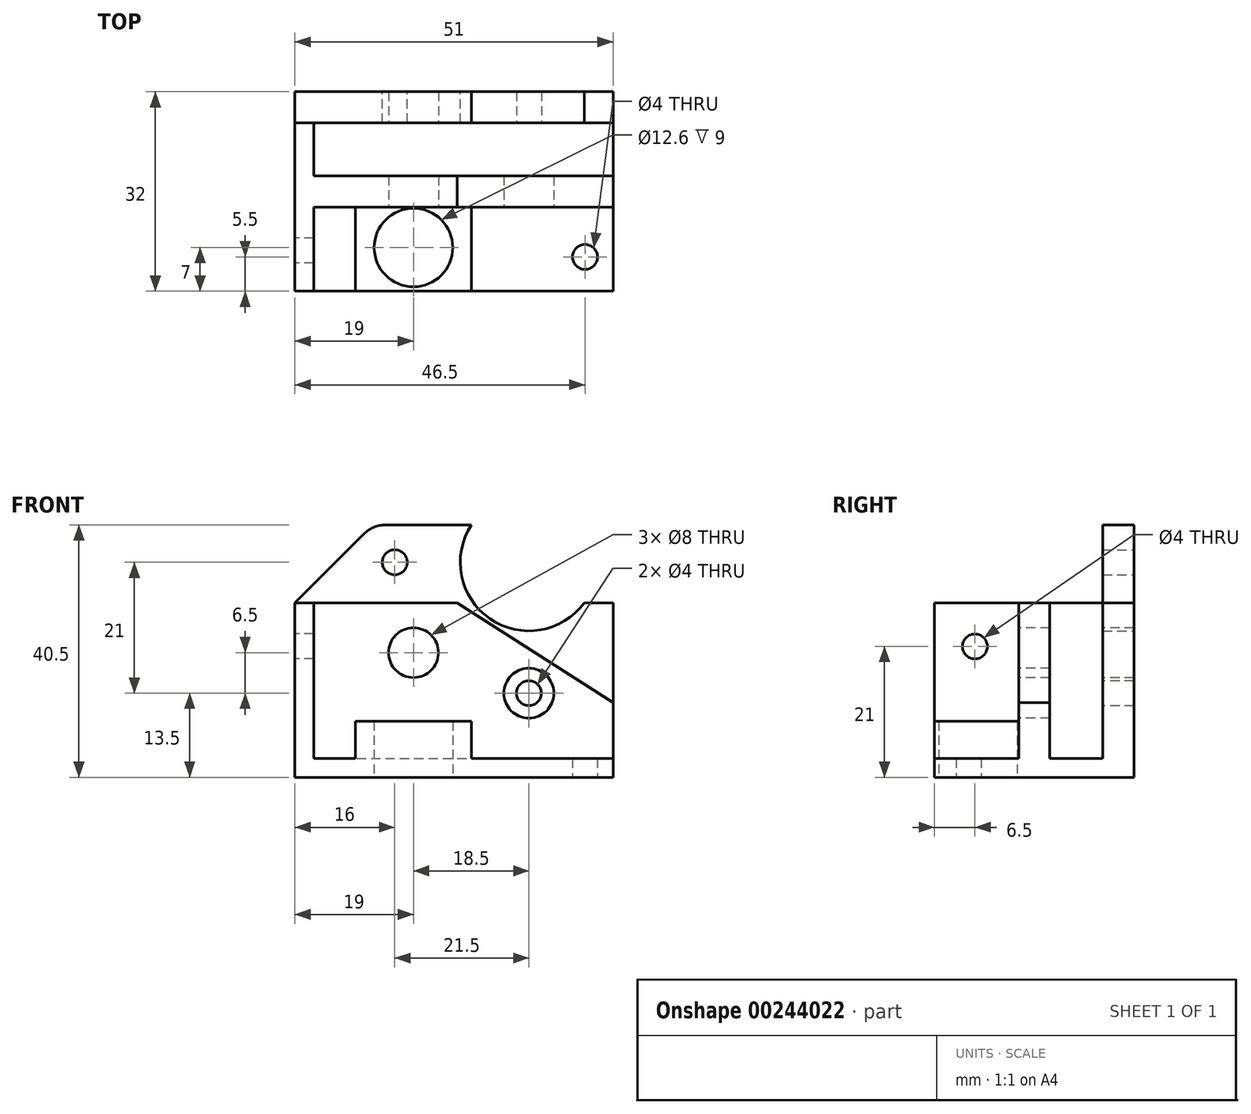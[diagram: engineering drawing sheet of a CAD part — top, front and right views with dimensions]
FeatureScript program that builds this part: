
annotation { "Feature Type Name" : "Feature", "Feature Type Description" : "" }
export const myFeature = defineFeature(function(context is Context, id is Id, definition is map)
    precondition{}
    {
        {
            var Q0;
            Q0=qCreatedBy(makeId("Top.planeOp"),FACE);
            var sketch = newSketch(context, id + "F0", { "sketchPlane" : qUnion([Q0])});
            skLineSegment(sketch, "E0.bottom", {"start": v(-25.5, 16) * mm, "end": v(25.5, 16) * mm});
            skLineSegment(sketch, "E0.top", {"start": v(-25.5, -16) * mm, "end": v(25.5, -16) * mm});
            skLineSegment(sketch, "E0.left", {"start": v(-25.5, 16) * mm, "end": v(-25.5, -16) * mm});
            skLineSegment(sketch, "E0.right", {"start": v(25.5, 16) * mm, "end": v(25.5, -16) * mm});
            skPoint(sketch, "E0.middle", {"position": v(0, 0) * mm});
            skCircle(sketch, "E1", {"center": v(21, -10.5) * mm, "radius": 2 * mm});
            skSolve(sketch);
        }
        {
            var Q0;
            Q0=makeQuery(id+"F0.imprint","IMPRINT",FACE,{"disambiguationData":[TD([[makeQuery(id+"F0.imprint","IMPRINT",EDGE,{"derivedFrom":sQuery(id+"F0.wireOp",EDGE,"E0.bottom")}),-1.0]])]});
            extrude(context, id + "F1", {"entities" : qUnion([Q0]), "depth" : 3 * mm});
        }
        {
            var Q0;
            Q0=makeQuery(id+"F1.opExtrude","CAP_FACE",FACE,{"disambiguationData":[OSD([sQuery(id+"F0.wireOp",EDGE,"E0.bottom"),sQuery(id+"F0.wireOp",EDGE,"E0.top"),sQuery(id+"F0.wireOp",EDGE,"E0.left"),sQuery(id+"F0.wireOp",EDGE,"E0.right"),sQuery(id+"F0.wireOp",EDGE,"E1")])],"isStart":false});
            var sketch = newSketch(context, id + "F2", { "sketchPlane" : qUnion([Q0])});
            skLineSegment(sketch, "E2", {"start": v(-22.5, 11) * mm, "end": v(25.5, 11) * mm});
            skLineSegment(sketch, "E3", {"start": v(-22.5, 2.5) * mm, "end": v(25.5, 2.5) * mm});
            skLineSegment(sketch, "E4.trimOffspring", {"start": v(-22.5, 2.5) * mm, "end": v(-22.5, 11) * mm});
            skLineSegment(sketch, "E5", {"start": v(-15.8, -2.5) * mm, "end": v(-15.8, -16) * mm});
            skLineSegment(sketch, "E6", {"start": v(2.8, -16) * mm, "end": v(2.8, -2.5) * mm});
            skLineSegment(sketch, "E7", {"start": v(-22.5, -2.5) * mm, "end": v(-22.5, -16) * mm});
            skLineSegment(sketch, "E8", {"start": v(-22.5, -2.5) * mm, "end": v(25.5, -2.5) * mm});
            skCircle(sketch, "E9", {"center": v(-6.5, -9) * mm, "radius": 6.3 * mm});
            skSolve(sketch);
        }
        {
            var Q0;
            {var subQ10=sQuery(id+"F2.wireOp",EDGE,"E2");Q0=makeQuery(id+"F2.imprint","IMPRINT",FACE,{"disambiguationData":[TD([[makeQuery(id+"F2.imprint","IMPRINT",EDGE,{"derivedFrom":subQ10}),1.0]])]});}
            extrude(context, id + "F3", {"entities" : qUnion([Q0]), "operationType" : NewBodyOperationType.ADD, "depth" : 25 * mm});
        }
        {
            var Q0;
            {var subQ1=sQuery(id+"F2.wireOp",EDGE,"E5");Q0=makeQuery(id+"F2.imprint","IMPRINT",FACE,{"disambiguationData":[TD([[makeQuery(id+"F2.imprint","IMPRINT",EDGE,{"derivedFrom":subQ1}),1.0]])]});}
            extrude(context, id + "F4", {"entities" : qUnion([Q0]), "operationType" : NewBodyOperationType.ADD, "depth" : 6 * mm});
        }
        {
            var Q0;
            {var subQ0=sQuery(id+"F0.wireOp",EDGE,"E1");var subQ1=sQuery(id+"F0.wireOp",EDGE,"E0.right");var subQ4=sQuery(id+"F0.wireOp",EDGE,"E0.top");var subQ5=sQuery(id+"F0.wireOp",EDGE,"E0.bottom");Q0=makeQuery(id+"F4.boolean.opBoolean","SPLIT",FACE,{"disambiguationData":[TD([makeQuery(id+"F4.opExtrude","SWEPT_FACE",FACE,{"disambiguationData":[OSD([sQuery(id+"F2.wireOp",EDGE,"E9")])]})])],"derivedFrom":makeQuery(id+"F3.boolean.opBoolean","SPLIT",FACE,{"disambiguationData":[TD([makeQuery(id+"F1.opExtrude","SWEPT_FACE",FACE,{"disambiguationData":[OSD([subQ4])]})])],"derivedFrom":makeQuery(id+"F1.opExtrude","CAP_FACE",FACE,{"disambiguationData":[OSD([subQ5,subQ4,sQuery(id+"F0.wireOp",EDGE,"E0.left"),subQ1,subQ0])],"isStart":false})})});}
            extrude(context, id + "F5", {"entities" : qUnion([Q0]), "operationType" : NewBodyOperationType.REMOVE, "endBound" : BoundingType.UP_TO_NEXT, "oppositeDirection" : true, "depth" : 25 * mm});
        }
        {
            var Q0;
            {var subQ0=sQuery(id+"F0.wireOp",EDGE,"E0.right");var subQ1=makeQuery(id+"F1.opExtrude","CAP_EDGE",EDGE,{"disambiguationData":[OSD([subQ0])],"isStart":false});Q0=makeQuery(id+"F3.opExtrude","CAP_EDGE",EDGE,{"disambiguationData":[OSD([subQ0]),TDD([makeQuery(id+"F2.imprint","IMPRINT",EDGE,{"disambiguationData":[TD([[makeQuery(id+"F2.imprint","INTERSECT",VERTEX,{"derivedFrom":[subQ1,sQuery(id+"F2.wireOp",EDGE,"E3")]}),-1.0]])],"derivedFrom":subQ1})])],"isStart":false});}
            chamfer(context, id + "F6", {"entities" : qUnion([Q0]), "chamferType" : ChamferType.TWO_OFFSETS, "width1" : 16 * mm, "oppositeDirection" : false, "width2" : 25 * mm, "tangentPropagation" : true});
        }
        {
            var Q0;
            Q0=makeQuery(id+"F3.opExtrude","SWEPT_FACE",FACE,{"disambiguationData":[OSD([sQuery(id+"F2.wireOp",EDGE,"E8")])]});
            var sketch = newSketch(context, id + "F7", { "sketchPlane" : qUnion([Q0])});
            skCircle(sketch, "E10", {"center": v(-6.5, 20) * mm, "radius": 4 * mm});
            skCircle(sketch, "E11", {"center": v(12, 13.5) * mm, "radius": 4 * mm});
            skCircle(sketch, "E12", {"center": v(12, 13.5) * mm, "radius": 2 * mm});
            skSolve(sketch);
        }
        {
            var Q0;
            Q0=makeQuery(id+"F7.imprint","IMPRINT",FACE,{"disambiguationData":[TD([[makeQuery(id+"F7.imprint","IMPRINT",EDGE,{"derivedFrom":sQuery(id+"F7.wireOp",EDGE,"E10")}),1.0]])]});
            extrude(context, id + "F8", {"entities" : qUnion([Q0]), "operationType" : NewBodyOperationType.REMOVE, "endBound" : BoundingType.THROUGH_ALL, "oppositeDirection" : true, "depth" : 25 * mm});
        }
        {
            var Q0;
            Q0=makeQuery(id+"F7.imprint","IMPRINT",FACE,{"disambiguationData":[TD([[makeQuery(id+"F7.imprint","IMPRINT",EDGE,{"derivedFrom":sQuery(id+"F7.wireOp",EDGE,"E12")}),1.0]])]});
            extrude(context, id + "F9", {"entities" : qUnion([Q0]), "operationType" : NewBodyOperationType.REMOVE, "endBound" : BoundingType.THROUGH_ALL, "oppositeDirection" : true, "depth" : 25 * mm});
        }
        {
            var Q0;
            Q0=makeQuery(id+"F7.imprint","IMPRINT",FACE,{"disambiguationData":[TD([[makeQuery(id+"F7.imprint","IMPRINT",EDGE,{"derivedFrom":sQuery(id+"F7.wireOp",EDGE,"E11")}),1.0]])]});
            extrude(context, id + "F10", {"entities" : qUnion([Q0]), "operationType" : NewBodyOperationType.REMOVE, "endBound" : BoundingType.UP_TO_NEXT, "oppositeDirection" : true, "depth" : 25 * mm});
        }
        {
            var Q0;
            Q0=makeQuery(id+"F3.opExtrude","CAP_FACE",FACE,{"disambiguationData":[OSD([sQuery(id+"F0.wireOp",EDGE,"E0.bottom"),sQuery(id+"F0.wireOp",EDGE,"E0.top"),sQuery(id+"F0.wireOp",EDGE,"E0.left"),sQuery(id+"F0.wireOp",EDGE,"E0.right"),sQuery(id+"F2.wireOp",EDGE,"E2"),sQuery(id+"F2.wireOp",EDGE,"E3"),sQuery(id+"F2.wireOp",EDGE,"E4.trimOffspring"),sQuery(id+"F2.wireOp",EDGE,"E7"),sQuery(id+"F2.wireOp",EDGE,"E8")])],"isStart":false});
            var sketch = newSketch(context, id + "F11", { "sketchPlane" : qUnion([Q0])});
            skLineSegment(sketch, "E13", {"start": v(-22.5, 11) * mm, "end": v(-25.5, 11) * mm});
            skSolve(sketch);
        }
        {
            var Q0;
            {var subQ5=sQuery(id+"F11.wireOp",EDGE,"E13");Q0=makeQuery(id+"F11.imprint","IMPRINT",FACE,{"disambiguationData":[TD([[makeQuery(id+"F11.imprint","IMPRINT",EDGE,{"derivedFrom":subQ5}),-1.0]])]});}
            extrude(context, id + "F12", {"entities" : qUnion([Q0]), "operationType" : NewBodyOperationType.ADD, "depth" : 12.5 * mm});
        }
        {
            var Q0;
            {var subQ0=sQuery(id+"F0.wireOp",EDGE,"E0.bottom");Q0=makeQuery(id+"F12.boolean.opBoolean","MERGE",FACE,{"derivedFrom":[makeQuery(id+"F3.boolean.opBoolean","MERGE",FACE,{"derivedFrom":[makeQuery(id+"F1.opExtrude","SWEPT_FACE",FACE,{"disambiguationData":[OSD([subQ0])]}),makeQuery(id+"F3.opExtrude","SWEPT_FACE",FACE,{"disambiguationData":[OSD([subQ0])]})]}),makeQuery(id+"F12.opExtrude","SWEPT_FACE",FACE,{"disambiguationData":[OSD([subQ0])]})]});}
            var sketch = newSketch(context, id + "F13", { "sketchPlane" : qUnion([Q0])});
            skCircle(sketch, "E14", {"center": v(9.5, 34.5) * mm, "radius": 2 * mm});
            skLineSegment(sketch, "E15", {"start": v(-12, 13.5) * mm, "end": v(-12, 47.77) * mm, "construction": true});
            skArc(sketch, "E16", {"start": v(-20.87, 28) * mm, "mid": v(-5.75, 25.45) * mm, "end": v(-2.78, 40.5) * mm});
            skLineSegment(sketch, "E17", {"start": v(-25.5, 28) * mm, "end": v(-20.87, 28) * mm});
            skPoint(sketch, "E18", {"position": v(-2.78, 40.5) * mm});
            skSolve(sketch);
        }
        {
            var Q0;
            Q0=makeQuery(id+"F13.imprint","IMPRINT",FACE,{"disambiguationData":[TD([[makeQuery(id+"F13.imprint","IMPRINT",EDGE,{"derivedFrom":sQuery(id+"F13.wireOp",EDGE,"E14")}),1.0]])]});
            var Q1;
            {var subQ0=sQuery(id+"F13.wireOp",EDGE,"E16");var subQ1=makeQuery(id+"F13.imprint","INTERSECT",VERTEX,{"derivedFrom":[subQ0,sQuery(id+"F13.wireOp",EDGE,"E17")]});Q1=makeQuery(id+"F13.imprint","IMPRINT",FACE,{"disambiguationData":[TD([[makeQuery(id+"F13.imprint","IMPRINT",EDGE,{"disambiguationData":[TD([[subQ1,1.0]])],"derivedFrom":subQ0}),1.0]])]});}
            var Q2;
            {var subQ0=sQuery(id+"F13.wireOp",EDGE,"E17");Q2=makeQuery(id+"F13.imprint","IMPRINT",FACE,{"disambiguationData":[TD([[makeQuery(id+"F13.imprint","IMPRINT",EDGE,{"derivedFrom":subQ0}),1.0]])]});}
            extrude(context, id + "F14", {"entities" : qUnion([Q0, Q1, Q2]), "operationType" : NewBodyOperationType.REMOVE, "endBound" : BoundingType.UP_TO_NEXT, "oppositeDirection" : true, "depth" : 25 * mm});
        }
        {
            var Q0;
            Q0=makeQuery(id+"F12.opExtrude","CAP_EDGE",EDGE,{"disambiguationData":[OSD([sQuery(id+"F0.wireOp",EDGE,"E0.left")])],"isStart":false});
            chamfer(context, id + "F15", {"entities" : qUnion([Q0]), "width" : 12.5 * mm, "tangentPropagation" : true});
        }
        {
            var Q0;
            Q0=makeQuery(id+"F14.boolean.opBoolean","COPY",EDGE,{"derivedFrom":makeQuery(id+"F14.opExtrude","SWEPT_EDGE",EDGE,{"disambiguationData":[OSD([sQuery(id+"F0.wireOp",EDGE,"E0.bottom"),sQuery(id+"F13.wireOp",EDGE,"E16")])]})});
            var Q1;
            {var subQ0=sQuery(id+"F0.wireOp",EDGE,"E0.left");Q1=makeQuery(id+"F15.opChamfer","BLEND_EDGE",EDGE,{"blendedFrom":[makeQuery(id+"F12.opExtrude","CAP_EDGE",EDGE,{"disambiguationData":[OSD([subQ0])],"isStart":false}),makeQuery(id+"F12.opExtrude","CAP_FACE",FACE,{"disambiguationData":[OSD([sQuery(id+"F0.wireOp",EDGE,"E0.bottom"),subQ0,sQuery(id+"F0.wireOp",EDGE,"E0.right"),sQuery(id+"F2.wireOp",EDGE,"E2"),sQuery(id+"F11.wireOp",EDGE,"E13")])],"isStart":false})],"blendedInto":[makeQuery(id+"F12.opExtrude","CAP_FACE",FACE,{"disambiguationData":[OSD([sQuery(id+"F0.wireOp",EDGE,"E0.bottom"),subQ0,sQuery(id+"F0.wireOp",EDGE,"E0.right"),sQuery(id+"F2.wireOp",EDGE,"E2"),sQuery(id+"F11.wireOp",EDGE,"E13")])],"isStart":false})]});}
            fillet(context, id + "F16", {"entities" : qUnion([Q0, Q1]), "radius" : 5 * mm, "tangentPropagation" : true, "allowEdgeOverflow" : false});
        }
        {
            var Q0;
            {var subQ0=sQuery(id+"F0.wireOp",EDGE,"E0.left");Q0=makeQuery(id+"F12.boolean.opBoolean","MERGE",FACE,{"derivedFrom":[makeQuery(id+"F3.boolean.opBoolean","MERGE",FACE,{"derivedFrom":[makeQuery(id+"F1.opExtrude","SWEPT_FACE",FACE,{"disambiguationData":[OSD([subQ0])]}),makeQuery(id+"F3.opExtrude","SWEPT_FACE",FACE,{"disambiguationData":[OSD([subQ0])]})]}),makeQuery(id+"F12.opExtrude","SWEPT_FACE",FACE,{"disambiguationData":[OSD([subQ0])]})]});}
            var sketch = newSketch(context, id + "F17", { "sketchPlane" : qUnion([Q0])});
            skCircle(sketch, "E19", {"center": v(9.5, 21) * mm, "radius": 2 * mm});
            skSolve(sketch);
        }
        {
            var Q0;
            Q0=makeQuery(id+"F17.imprint","IMPRINT",FACE,{"disambiguationData":[TD([[makeQuery(id+"F17.imprint","IMPRINT",EDGE,{"derivedFrom":sQuery(id+"F17.wireOp",EDGE,"E19")}),1.0]])]});
            extrude(context, id + "F18", {"entities" : qUnion([Q0]), "operationType" : NewBodyOperationType.REMOVE, "endBound" : BoundingType.UP_TO_NEXT, "oppositeDirection" : true, "depth" : 25 * mm});
        }
    });
